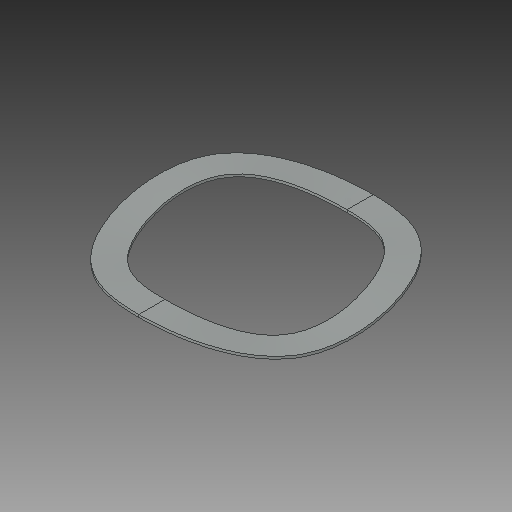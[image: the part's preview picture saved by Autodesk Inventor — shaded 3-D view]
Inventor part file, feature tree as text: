
AUTODESK INVENTOR PART (.ipt)
format: ipt  version: 2018 (Build 220112000, 112)  size: 123,904 bytes
history: native  units: in
note: dims shown in document units (in); Inventor stores cm internally (conversion verified against a paired STEP export)
features: loft x1
ambient origin geometry x8: Origin, YZ Plane, XZ Plane, XY Plane, X Axis, Y Axis, Z Axis, Center Point
bodies: Solid1 (feature_tree)
feature tree (1):
  loft  "Loft1"
